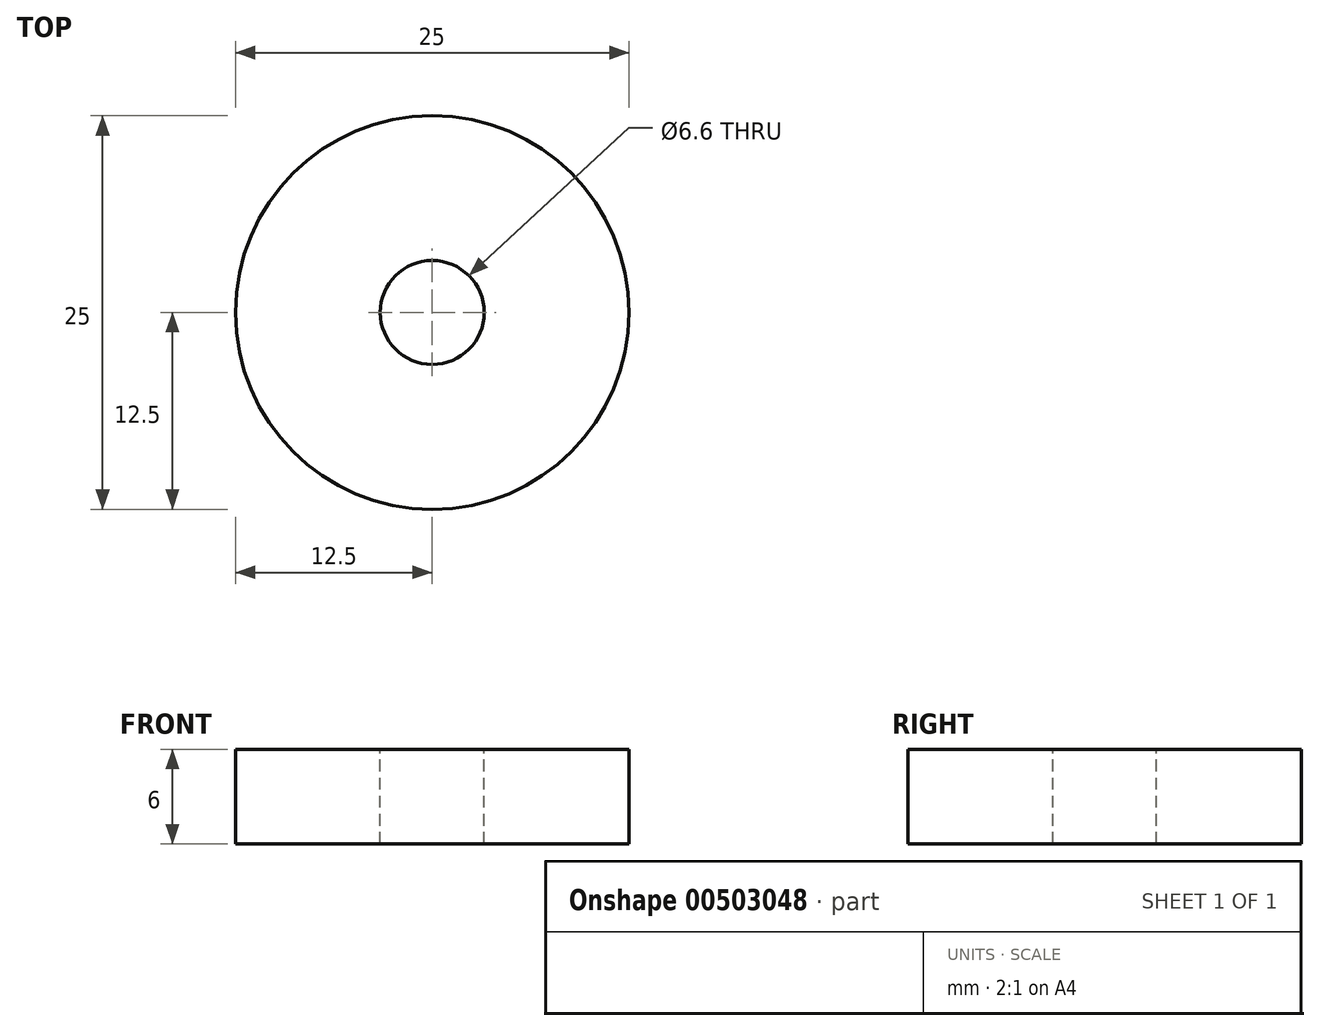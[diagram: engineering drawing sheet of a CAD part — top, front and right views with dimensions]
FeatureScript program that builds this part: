
annotation { "Feature Type Name" : "Feature", "Feature Type Description" : "" }
export const myFeature = defineFeature(function(context is Context, id is Id, definition is map)
    precondition{}
    {
        {
            var Q0;
            Q0=qCreatedBy(makeId("Top.planeOp"),FACE);
            var sketch = newSketch(context, id + "F0", { "sketchPlane" : qUnion([Q0])});
            skCircle(sketch, "E0", {"center": v(0, 0) * mm, "radius": 12.5 * mm});
            skSolve(sketch);
        }
        {
            var Q0;
            Q0=makeQuery(id+"F0.imprint","IMPRINT",FACE,{"disambiguationData":[TD([[makeQuery(id+"F0.imprint","IMPRINT",EDGE,{"derivedFrom":sQuery(id+"F0.wireOp",EDGE,"E0")}),1.0]])]});
            extrude(context, id + "F1", {"entities" : qUnion([Q0]), "depth" : 6 * mm});
        }
        {
            var Q0;
            Q0=makeQuery(id+"F1.opExtrude","CAP_FACE",FACE,{"disambiguationData":[OSD([sQuery(id+"F0.wireOp",EDGE,"E0")])],"isStart":false});
            var sketch = newSketch(context, id + "F2", { "sketchPlane" : qUnion([Q0])});
            skPoint(sketch, "E1", {"position": v(0, 0) * mm});
            skSolve(sketch);
        }
        {
            var Q0;
            Q0=sQuery(id+"F2.wireOp",VERTEX,"E1");
            var Q1;
            Q1=makeQuery(id+"F1.opExtrude","SWEPT_BODY",BODY,{"disambiguationData":[OSD([sQuery(id+"F0.wireOp",EDGE,"E0")])]});
            hole(context, id + "F3", {"style" : HoleStyle.SIMPLE, "endStyle" : HoleEndStyle.BLIND, "standardTappedOrClearance" : lookupTablePath({ "standard" : "ISO", "fit" : "Normal", "size" : "M6", "type" : "Clearance" }), "standardBlindInLast" : lookupTablePath({ "fit" : "Standard", "standard" : "ISO", "size" : "M6", "type" : "Clearance" }), "holeDiameter" : 6.6 * mm, "holeDepth" : 15 * mm, "isTappedThrough" : true, "tappedDepth" : 12 * mm, "tapClearance" : 3, "startFromSketch" : true, "locations" : qUnion([Q0]), "scope" : qUnion([Q1])});
        }
    });
